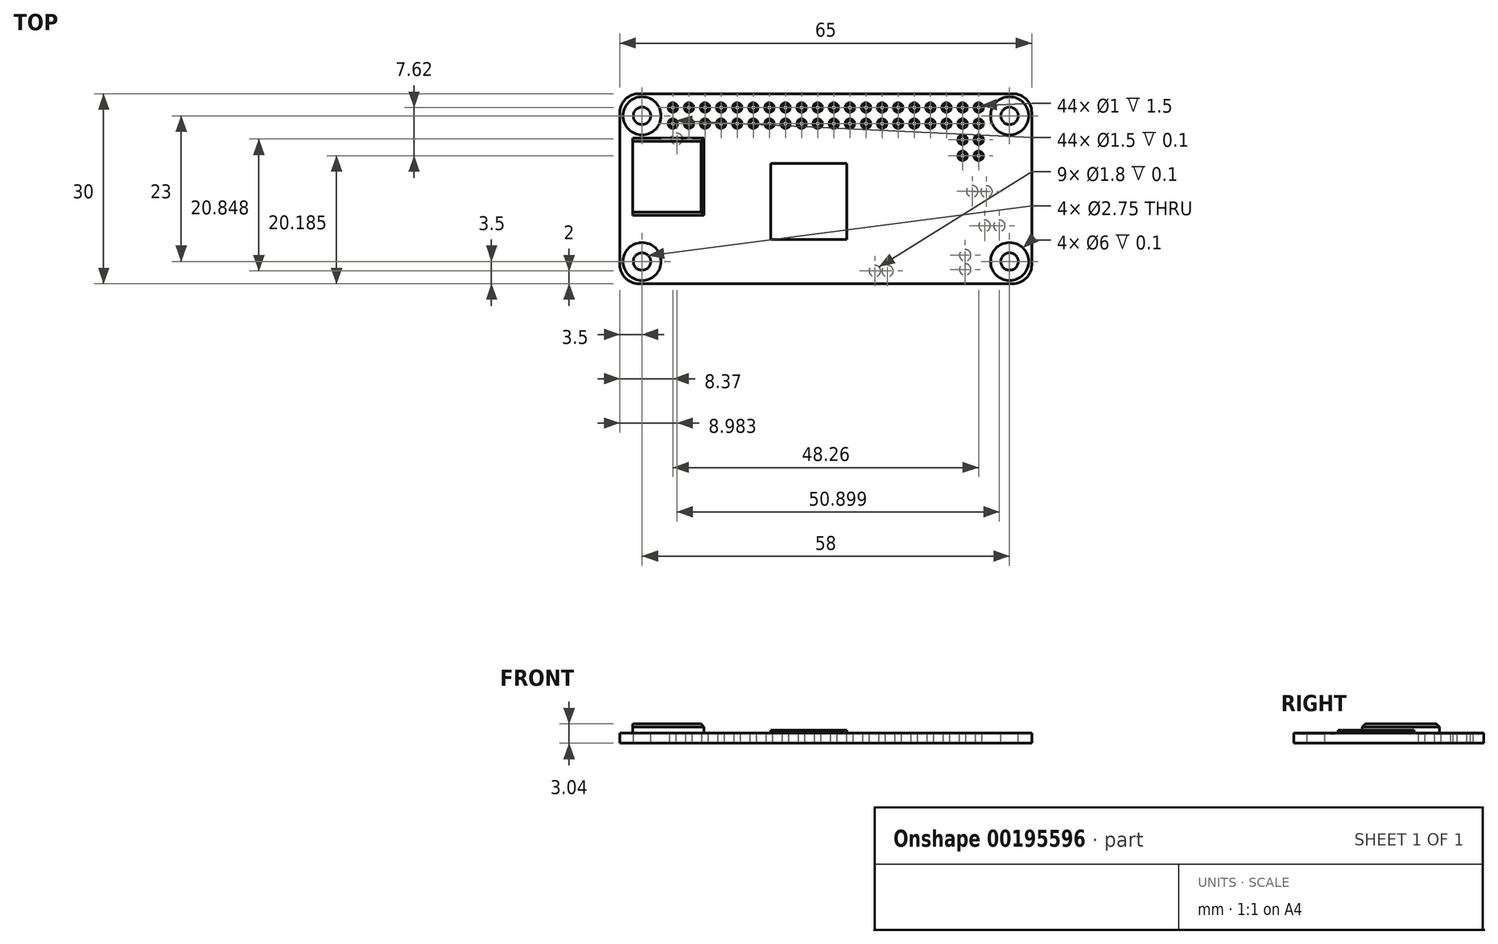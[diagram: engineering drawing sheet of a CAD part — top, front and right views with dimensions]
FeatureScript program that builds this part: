
annotation { "Feature Type Name" : "Feature", "Feature Type Description" : "" }
export const myFeature = defineFeature(function(context is Context, id is Id, definition is map)
    precondition{}
    {
        {
            var Q0;
            Q0=qCreatedBy(makeId("Top.planeOp"),FACE);
            var sketch = newSketch(context, id + "F0", { "sketchPlane" : qUnion([Q0])});
            skLineSegment(sketch, "E0.bottom", {"start": v(-29.5, 15) * mm, "end": v(29.5, 15) * mm});
            skLineSegment(sketch, "E0.top", {"start": v(-29.5, -15) * mm, "end": v(29.5, -15) * mm});
            skLineSegment(sketch, "E0.left", {"start": v(-32.5, 12) * mm, "end": v(-32.5, -12) * mm});
            skLineSegment(sketch, "E0.right", {"start": v(32.5, 12) * mm, "end": v(32.5, -12) * mm});
            skPoint(sketch, "E1.visualSharp", {"position": v(-32.5, 15) * mm});
            skArc(sketch, "E1.filletArc", {"start": v(-29.5, 15) * mm, "mid": v(-31.62, 14.12) * mm, "end": v(-32.5, 12) * mm});
            skPoint(sketch, "E2.visualSharp", {"position": v(32.5, 15) * mm});
            skArc(sketch, "E2.filletArc", {"start": v(32.5, 12) * mm, "mid": v(31.62, 14.12) * mm, "end": v(29.5, 15) * mm});
            skPoint(sketch, "E3.visualSharp", {"position": v(32.5, -15) * mm});
            skArc(sketch, "E3.filletArc", {"start": v(29.5, -15) * mm, "mid": v(31.62, -14.12) * mm, "end": v(32.5, -12) * mm});
            skPoint(sketch, "E4.visualSharp", {"position": v(-32.5, -15) * mm});
            skArc(sketch, "E4.filletArc", {"start": v(-32.5, -12) * mm, "mid": v(-31.62, -14.12) * mm, "end": v(-29.5, -15) * mm});
            skPoint(sketch, "E5", {"position": v(-29, 11.5) * mm});
            skPoint(sketch, "E6", {"position": v(-24.13, 12.8) * mm});
            skPoint(sketch, "E7.0.1.0", {"position": v(-24.13, 10.26) * mm});
            skPoint(sketch, "E7.1.0.0", {"position": v(-21.59, 12.8) * mm});
            skPoint(sketch, "E7.1.1.0", {"position": v(-21.59, 10.26) * mm});
            skPoint(sketch, "E7.2.0.0", {"position": v(-19.05, 12.8) * mm});
            skPoint(sketch, "E7.2.1.0", {"position": v(-19.05, 10.26) * mm});
            skPoint(sketch, "E7.3.0.0", {"position": v(-16.5, 12.8) * mm});
            skPoint(sketch, "E7.3.1.0", {"position": v(-16.5, 10.26) * mm});
            skPoint(sketch, "E7.4.0.0", {"position": v(-13.97, 12.8) * mm});
            skPoint(sketch, "E7.4.1.0", {"position": v(-13.97, 10.26) * mm});
            skPoint(sketch, "E7.5.0.0", {"position": v(-11.43, 12.8) * mm});
            skPoint(sketch, "E7.5.1.0", {"position": v(-11.43, 10.26) * mm});
            skPoint(sketch, "E7.6.0.0", {"position": v(-8.89, 12.8) * mm});
            skPoint(sketch, "E7.6.1.0", {"position": v(-8.89, 10.26) * mm});
            skPoint(sketch, "E7.7.0.0", {"position": v(-6.35, 12.8) * mm});
            skPoint(sketch, "E7.7.1.0", {"position": v(-6.35, 10.26) * mm});
            skPoint(sketch, "E7.8.0.0", {"position": v(-3.8, 12.8) * mm});
            skPoint(sketch, "E7.8.1.0", {"position": v(-3.8, 10.26) * mm});
            skPoint(sketch, "E7.9.0.0", {"position": v(-1.27, 12.8) * mm});
            skPoint(sketch, "E7.9.1.0", {"position": v(-1.27, 10.26) * mm});
            skPoint(sketch, "E7.10.0.0", {"position": v(1.27, 12.8) * mm});
            skPoint(sketch, "E7.10.1.0", {"position": v(1.27, 10.26) * mm});
            skPoint(sketch, "E7.11.0.0", {"position": v(3.81, 12.8) * mm});
            skPoint(sketch, "E7.11.1.0", {"position": v(3.81, 10.26) * mm});
            skPoint(sketch, "E7.12.0.0", {"position": v(6.35, 12.8) * mm});
            skPoint(sketch, "E7.12.1.0", {"position": v(6.35, 10.26) * mm});
            skPoint(sketch, "E7.13.0.0", {"position": v(8.9, 12.8) * mm});
            skPoint(sketch, "E7.13.1.0", {"position": v(8.9, 10.26) * mm});
            skPoint(sketch, "E7.14.0.0", {"position": v(11.43, 12.8) * mm});
            skPoint(sketch, "E7.14.1.0", {"position": v(11.43, 10.26) * mm});
            skPoint(sketch, "E7.15.0.0", {"position": v(13.97, 12.8) * mm});
            skPoint(sketch, "E7.15.1.0", {"position": v(13.97, 10.26) * mm});
            skPoint(sketch, "E7.16.0.0", {"position": v(16.51, 12.8) * mm});
            skPoint(sketch, "E7.16.1.0", {"position": v(16.51, 10.26) * mm});
            skPoint(sketch, "E7.17.0.0", {"position": v(19.05, 12.8) * mm});
            skPoint(sketch, "E7.17.1.0", {"position": v(19.05, 10.26) * mm});
            skPoint(sketch, "E7.18.0.0", {"position": v(21.6, 12.8) * mm});
            skPoint(sketch, "E7.18.1.0", {"position": v(21.6, 10.26) * mm});
            skPoint(sketch, "E7.19.0.0", {"position": v(24.13, 12.8) * mm});
            skPoint(sketch, "E7.19.1.0", {"position": v(24.13, 10.26) * mm});
            skLineSegment(sketch, "E7.direction1", {"start": v(-24.13, 12.8) * mm, "end": v(-21.59, 12.8) * mm, "construction": true});
            skLineSegment(sketch, "E7.direction2", {"start": v(-24.13, 12.8) * mm, "end": v(-24.13, 10.26) * mm, "construction": true});
            skPoint(sketch, "E8.0.1.0", {"position": v(-29, -11.5) * mm});
            skPoint(sketch, "E8.1.0.0", {"position": v(29, 11.5) * mm});
            skPoint(sketch, "E8.1.1.0", {"position": v(29, -11.5) * mm});
            skLineSegment(sketch, "E8.direction1", {"start": v(-29, 11.5) * mm, "end": v(29, 11.5) * mm, "construction": true});
            skLineSegment(sketch, "E8.direction2", {"start": v(-29, 11.5) * mm, "end": v(-29, -11.5) * mm, "construction": true});
            skPoint(sketch, "E9.0.1.0", {"position": v(24.13, 7.72) * mm});
            skPoint(sketch, "E9.0.1.1", {"position": v(21.6, 7.72) * mm});
            skPoint(sketch, "E9.0.2.0", {"position": v(24.13, 5.18) * mm});
            skPoint(sketch, "E9.0.2.1", {"position": v(21.6, 5.18) * mm});
            skLineSegment(sketch, "E9.direction1", {"start": v(21.6, 10.26) * mm, "end": v(38.2, 10.26) * mm, "construction": true});
            skLineSegment(sketch, "E9.direction2", {"start": v(21.6, 10.26) * mm, "end": v(21.6, 7.72) * mm, "construction": true});
            skSolve(sketch);
        }
        {
            var Q0;
            Q0 = qSketchRegion(id + "F0", true);
            extrude(context, id + "F1", {"entities" : qUnion([Q0]), "oppositeDirection" : true, "depth" : 1.6 * mm});
        }
        {
            var Q0;
            Q0=sQuery(id+"F0.wireOp",VERTEX,"E8.0.1.0");
            var Q1;
            Q1=sQuery(id+"F0.wireOp",VERTEX,"E5");
            var Q2;
            Q2=sQuery(id+"F0.wireOp",VERTEX,"E8.1.0.0");
            var Q3;
            Q3=sQuery(id+"F0.wireOp",VERTEX,"E8.1.1.0");
            var Q4;
            Q4=makeQuery(id+"F1.opExtrude","SWEPT_BODY",BODY,{"disambiguationData":[OSD([sQuery(id+"F0.wireOp",EDGE,"E0.bottom"),sQuery(id+"F0.wireOp",EDGE,"E0.top"),sQuery(id+"F0.wireOp",EDGE,"E0.left"),sQuery(id+"F0.wireOp",EDGE,"E0.right"),sQuery(id+"F0.wireOp",EDGE,"E1.filletArc"),sQuery(id+"F0.wireOp",EDGE,"E2.filletArc"),sQuery(id+"F0.wireOp",EDGE,"E3.filletArc"),sQuery(id+"F0.wireOp",EDGE,"E4.filletArc")])]});
            hole(context, id + "F2", {"style" : HoleStyle.C_BORE, "endStyle" : HoleEndStyle.THROUGH, "holeDiameter" : 2.75 * mm, "cBoreDiameter" : 6 * mm, "cBoreDepth" : 0.1 * mm, "locations" : qUnion([Q0, Q1, Q2, Q3]), "scope" : qUnion([Q4]), "isTappedThrough" : true});
        }
        {
            var Q0;
            Q0=sQuery(id+"F0.wireOp",VERTEX,"E6");
            var Q1;
            Q1=sQuery(id+"F0.wireOp",VERTEX,"E7.1.0.0");
            var Q2;
            Q2=sQuery(id+"F0.wireOp",VERTEX,"E7.0.1.0");
            var Q3;
            Q3=sQuery(id+"F0.wireOp",VERTEX,"E7.1.1.0");
            var Q4;
            Q4=sQuery(id+"F0.wireOp",VERTEX,"E7.2.1.0");
            var Q5;
            Q5=sQuery(id+"F0.wireOp",VERTEX,"E7.2.0.0");
            var Q6;
            Q6=sQuery(id+"F0.wireOp",VERTEX,"E7.3.0.0");
            var Q7;
            Q7=sQuery(id+"F0.wireOp",VERTEX,"E7.3.1.0");
            var Q8;
            Q8=sQuery(id+"F0.wireOp",VERTEX,"E7.4.1.0");
            var Q9;
            Q9=sQuery(id+"F0.wireOp",VERTEX,"E7.4.0.0");
            var Q10;
            Q10=sQuery(id+"F0.wireOp",VERTEX,"E7.5.0.0");
            var Q11;
            Q11=sQuery(id+"F0.wireOp",VERTEX,"E7.5.1.0");
            var Q12;
            Q12=sQuery(id+"F0.wireOp",VERTEX,"E7.6.1.0");
            var Q13;
            Q13=sQuery(id+"F0.wireOp",VERTEX,"E7.6.0.0");
            var Q14;
            Q14=sQuery(id+"F0.wireOp",VERTEX,"E7.7.0.0");
            var Q15;
            Q15=sQuery(id+"F0.wireOp",VERTEX,"E7.7.1.0");
            var Q16;
            Q16=sQuery(id+"F0.wireOp",VERTEX,"E7.8.0.0");
            var Q17;
            Q17=sQuery(id+"F0.wireOp",VERTEX,"E7.8.1.0");
            var Q18;
            Q18=sQuery(id+"F0.wireOp",VERTEX,"E7.9.0.0");
            var Q19;
            Q19=sQuery(id+"F0.wireOp",VERTEX,"E7.9.1.0");
            var Q20;
            Q20=sQuery(id+"F0.wireOp",VERTEX,"E7.10.0.0");
            var Q21;
            Q21=sQuery(id+"F0.wireOp",VERTEX,"E7.10.1.0");
            var Q22;
            Q22=sQuery(id+"F0.wireOp",VERTEX,"E7.11.0.0");
            var Q23;
            Q23=sQuery(id+"F0.wireOp",VERTEX,"E7.11.1.0");
            var Q24;
            Q24=sQuery(id+"F0.wireOp",VERTEX,"E7.12.0.0");
            var Q25;
            Q25=sQuery(id+"F0.wireOp",VERTEX,"E7.12.1.0");
            var Q26;
            Q26=sQuery(id+"F0.wireOp",VERTEX,"E7.13.0.0");
            var Q27;
            Q27=sQuery(id+"F0.wireOp",VERTEX,"E7.13.1.0");
            var Q28;
            Q28=sQuery(id+"F0.wireOp",VERTEX,"E7.14.0.0");
            var Q29;
            Q29=sQuery(id+"F0.wireOp",VERTEX,"E7.14.1.0");
            var Q30;
            Q30=sQuery(id+"F0.wireOp",VERTEX,"E7.15.0.0");
            var Q31;
            Q31=sQuery(id+"F0.wireOp",VERTEX,"E7.15.1.0");
            var Q32;
            Q32=sQuery(id+"F0.wireOp",VERTEX,"E7.16.0.0");
            var Q33;
            Q33=sQuery(id+"F0.wireOp",VERTEX,"E7.16.1.0");
            var Q34;
            Q34=sQuery(id+"F0.wireOp",VERTEX,"E7.17.0.0");
            var Q35;
            Q35=sQuery(id+"F0.wireOp",VERTEX,"E7.17.1.0");
            var Q36;
            Q36=sQuery(id+"F0.wireOp",VERTEX,"E7.18.0.0");
            var Q37;
            Q37=sQuery(id+"F0.wireOp",VERTEX,"E7.18.1.0");
            var Q38;
            Q38=sQuery(id+"F0.wireOp",VERTEX,"E7.19.0.0");
            var Q39;
            Q39=sQuery(id+"F0.wireOp",VERTEX,"E7.19.1.0");
            var Q40;
            Q40=sQuery(id+"F0.wireOp",VERTEX,"E9.0.1.1");
            var Q41;
            Q41=sQuery(id+"F0.wireOp",VERTEX,"E9.0.1.0");
            var Q42;
            Q42=sQuery(id+"F0.wireOp",VERTEX,"E9.0.2.0");
            var Q43;
            Q43=sQuery(id+"F0.wireOp",VERTEX,"E9.0.2.1");
            var Q44;
            Q44=makeQuery(id+"F1.opExtrude","SWEPT_BODY",BODY,{"disambiguationData":[OSD([sQuery(id+"F0.wireOp",EDGE,"E0.bottom"),sQuery(id+"F0.wireOp",EDGE,"E0.top"),sQuery(id+"F0.wireOp",EDGE,"E0.left"),sQuery(id+"F0.wireOp",EDGE,"E0.right"),sQuery(id+"F0.wireOp",EDGE,"E1.filletArc"),sQuery(id+"F0.wireOp",EDGE,"E2.filletArc"),sQuery(id+"F0.wireOp",EDGE,"E3.filletArc"),sQuery(id+"F0.wireOp",EDGE,"E4.filletArc")])]});
            hole(context, id + "F3", {"style" : HoleStyle.C_BORE, "endStyle" : HoleEndStyle.THROUGH, "holeDiameter" : 1 * mm, "cBoreDiameter" : 1.5 * mm, "cBoreDepth" : 0.1 * mm, "locations" : qUnion([Q0, Q1, Q2, Q3, Q4, Q5, Q6, Q7, Q8, Q9, Q10, Q11, Q12, Q13, Q14, Q15, Q16, Q17, Q18, Q19, Q20, Q21, Q22, Q23, Q24, Q25, Q26, Q27, Q28, Q29, Q30, Q31, Q32, Q33, Q34, Q35, Q36, Q37, Q38, Q39, Q40, Q41, Q42, Q43]), "scope" : qUnion([Q44]), "isTappedThrough" : true});
        }
        {
            var Q0;
            Q0=makeQuery(id+"F0.imprint","IMPRINT",FACE,{"disambiguationData":[TD([[makeQuery(id+"F0.imprint","IMPRINT",EDGE,{"derivedFrom":sQuery(id+"F0.wireOp",EDGE,"E0.bottom")}),-1.0]])]});
            var sketch = newSketch(context, id + "F4", { "sketchPlane" : qUnion([Q0])});
            skLineSegment(sketch, "E10.bottom", {"start": v(-8.7, 4) * mm, "end": v(3.3, 4) * mm});
            skLineSegment(sketch, "E10.top", {"start": v(-8.7, -8) * mm, "end": v(3.3, -8) * mm});
            skLineSegment(sketch, "E10.left", {"start": v(-8.7, 4) * mm, "end": v(-8.7, -8) * mm});
            skLineSegment(sketch, "E10.right", {"start": v(3.3, 4) * mm, "end": v(3.3, -8) * mm});
            skLineSegment(sketch, "E11.bottom", {"start": v(-19.2, 8) * mm, "end": v(-30.5, 8) * mm});
            skLineSegment(sketch, "E11.top", {"start": v(-19.2, -4.2) * mm, "end": v(-30.5, -4.2) * mm});
            skLineSegment(sketch, "E11.left", {"start": v(-19.2, 8) * mm, "end": v(-19.2, -4.2) * mm});
            skLineSegment(sketch, "E11.right", {"start": v(-30.5, 8) * mm, "end": v(-30.5, -4.2) * mm});
            skSolve(sketch);
        }
        {
            var Q0;
            Q0=makeQuery(id+"F4.imprint","IMPRINT",FACE,{"disambiguationData":[TD([[makeQuery(id+"F4.imprint","IMPRINT",EDGE,{"derivedFrom":sQuery(id+"F4.wireOp",EDGE,"E10.bottom")}),-1.0]])]});
            extrude(context, id + "F5", {"entities" : qUnion([Q0]), "operationType" : NewBodyOperationType.ADD, "depth" : 0.45 * mm});
        }
        {
            var Q0;
            Q0=makeQuery(id+"F4.imprint","IMPRINT",FACE,{"disambiguationData":[TD([[makeQuery(id+"F4.imprint","IMPRINT",EDGE,{"derivedFrom":sQuery(id+"F4.wireOp",EDGE,"E11.bottom")}),1.0]])]});
            extrude(context, id + "F6", {"entities" : qUnion([Q0]), "operationType" : NewBodyOperationType.ADD, "depth" : 1.44 * mm});
        }
        {
            var Q0;
            Q0=makeQuery(id+"F1.opExtrude","CAP_FACE",FACE,{"disambiguationData":[OSD([sQuery(id+"F0.wireOp",EDGE,"E0.bottom"),sQuery(id+"F0.wireOp",EDGE,"E0.top"),sQuery(id+"F0.wireOp",EDGE,"E0.left"),sQuery(id+"F0.wireOp",EDGE,"E0.right"),sQuery(id+"F0.wireOp",EDGE,"E1.filletArc"),sQuery(id+"F0.wireOp",EDGE,"E2.filletArc"),sQuery(id+"F0.wireOp",EDGE,"E3.filletArc"),sQuery(id+"F0.wireOp",EDGE,"E4.filletArc")])],"isStart":false});
            var sketch = newSketch(context, id + "F7", { "sketchPlane" : qUnion([Q0])});
            skCircle(sketch, "E12", {"center": v(25.06, 5.85) * mm, "radius": 0.9 * mm});
            skCircle(sketch, "E13", {"center": v(25.38, 0.46) * mm, "radius": 0.9 * mm});
            skCircle(sketch, "E14", {"center": v(22, 12.75) * mm, "radius": 0.9 * mm});
            skCircle(sketch, "E15", {"center": v(-23.52, -7.85) * mm, "radius": 0.9 * mm});
            skCircle(sketch, "E16", {"center": v(22, 10.5) * mm, "radius": 0.9 * mm});
            skCircle(sketch, "E17", {"center": v(27.38, 5.84) * mm, "radius": 0.9 * mm});
            skCircle(sketch, "E18", {"center": v(23.12, 0.42) * mm, "radius": 0.9 * mm});
            skCircle(sketch, "E19", {"center": v(9.75, 13) * mm, "radius": 0.9 * mm});
            skCircle(sketch, "E20", {"center": v(7.75, 13) * mm, "radius": 0.9 * mm});
            skSolve(sketch);
        }
        {
            var Q0;
            Q0=makeQuery(id+"F7.imprint","IMPRINT",FACE,{"disambiguationData":[TD([[makeQuery(id+"F7.imprint","IMPRINT",EDGE,{"derivedFrom":sQuery(id+"F7.wireOp",EDGE,"E12")}),1.0]])]});
            var Q1;
            Q1=makeQuery(id+"F7.imprint","IMPRINT",FACE,{"disambiguationData":[TD([[makeQuery(id+"F7.imprint","IMPRINT",EDGE,{"derivedFrom":sQuery(id+"F7.wireOp",EDGE,"E13")}),1.0]])]});
            var Q2;
            Q2=makeQuery(id+"F7.imprint","IMPRINT",FACE,{"disambiguationData":[TD([[makeQuery(id+"F7.imprint","IMPRINT",EDGE,{"derivedFrom":sQuery(id+"F7.wireOp",EDGE,"E15")}),1.0]])]});
            var Q3;
            Q3=makeQuery(id+"F7.imprint","IMPRINT",FACE,{"disambiguationData":[TD([[makeQuery(id+"F7.imprint","IMPRINT",EDGE,{"derivedFrom":sQuery(id+"F7.wireOp",EDGE,"E14")}),1.0]])]});
            var Q4;
            Q4=sQuery(id+"F7.wireOp",EDGE,"E13");
            var Q5;
            Q5=sQuery(id+"F7.wireOp",EDGE,"E12");
            var Q6;
            Q6=sQuery(id+"F7.wireOp",EDGE,"E14");
            var Q7;
            Q7=sQuery(id+"F7.wireOp",EDGE,"E15");
            extrude(context, id + "F8", {"entities" : qUnion([Q0, Q1, Q2, Q3]), "operationType" : NewBodyOperationType.REMOVE, "surfaceEntities" : qUnion([Q4, Q5, Q6, Q7]), "oppositeDirection" : true, "depth" : 0.1 * mm});
        }
        {
            var Q0;
            Q0=makeQuery(id+"F7.imprint","IMPRINT",FACE,{"disambiguationData":[TD([[makeQuery(id+"F7.imprint","IMPRINT",EDGE,{"derivedFrom":sQuery(id+"F7.wireOp",EDGE,"E18")}),1.0]])]});
            var Q1;
            Q1=makeQuery(id+"F7.imprint","IMPRINT",FACE,{"disambiguationData":[TD([[makeQuery(id+"F7.imprint","IMPRINT",EDGE,{"derivedFrom":sQuery(id+"F7.wireOp",EDGE,"E17")}),1.0]])]});
            var Q2;
            Q2=makeQuery(id+"F7.imprint","IMPRINT",FACE,{"disambiguationData":[TD([[makeQuery(id+"F7.imprint","IMPRINT",EDGE,{"derivedFrom":sQuery(id+"F7.wireOp",EDGE,"E19")}),1.0]])]});
            var Q3;
            Q3=makeQuery(id+"F7.imprint","IMPRINT",FACE,{"disambiguationData":[TD([[makeQuery(id+"F7.imprint","IMPRINT",EDGE,{"derivedFrom":sQuery(id+"F7.wireOp",EDGE,"E16")}),1.0]])]});
            var Q4;
            Q4=makeQuery(id+"F7.imprint","IMPRINT",FACE,{"disambiguationData":[TD([[makeQuery(id+"F7.imprint","IMPRINT",EDGE,{"derivedFrom":sQuery(id+"F7.wireOp",EDGE,"E20")}),1.0]])]});
            var Q5;
            Q5=sQuery(id+"F7.wireOp",EDGE,"E18");
            var Q6;
            Q6=sQuery(id+"F7.wireOp",EDGE,"E17");
            var Q7;
            Q7=sQuery(id+"F7.wireOp",EDGE,"E16");
            var Q8;
            Q8=sQuery(id+"F7.wireOp",EDGE,"E19");
            var Q9;
            Q9=sQuery(id+"F7.wireOp",EDGE,"E20");
            extrude(context, id + "F9", {"entities" : qUnion([Q0, Q1, Q2, Q3, Q4]), "operationType" : NewBodyOperationType.REMOVE, "surfaceEntities" : qUnion([Q5, Q6, Q7, Q8, Q9]), "oppositeDirection" : true, "depth" : 0.1 * mm});
        }
        {
            var Q0;
            Q0=makeQuery(id+"F6.opExtrude","CAP_EDGE",EDGE,{"disambiguationData":[OSD([sQuery(id+"F4.wireOp",EDGE,"E11.top")])],"isStart":false});
            var Q1;
            Q1=makeQuery(id+"F6.opExtrude","CAP_EDGE",EDGE,{"disambiguationData":[OSD([sQuery(id+"F4.wireOp",EDGE,"E11.bottom")])],"isStart":false});
            var Q2;
            Q2=makeQuery(id+"F6.opExtrude","CAP_EDGE",EDGE,{"disambiguationData":[OSD([sQuery(id+"F4.wireOp",EDGE,"E11.left")])],"isStart":false});
            chamfer(context, id + "F10", {"entities" : qUnion([Q0, Q1, Q2]), "width" : 0.5 * mm, "tangentPropagation" : true});
        }
    });
